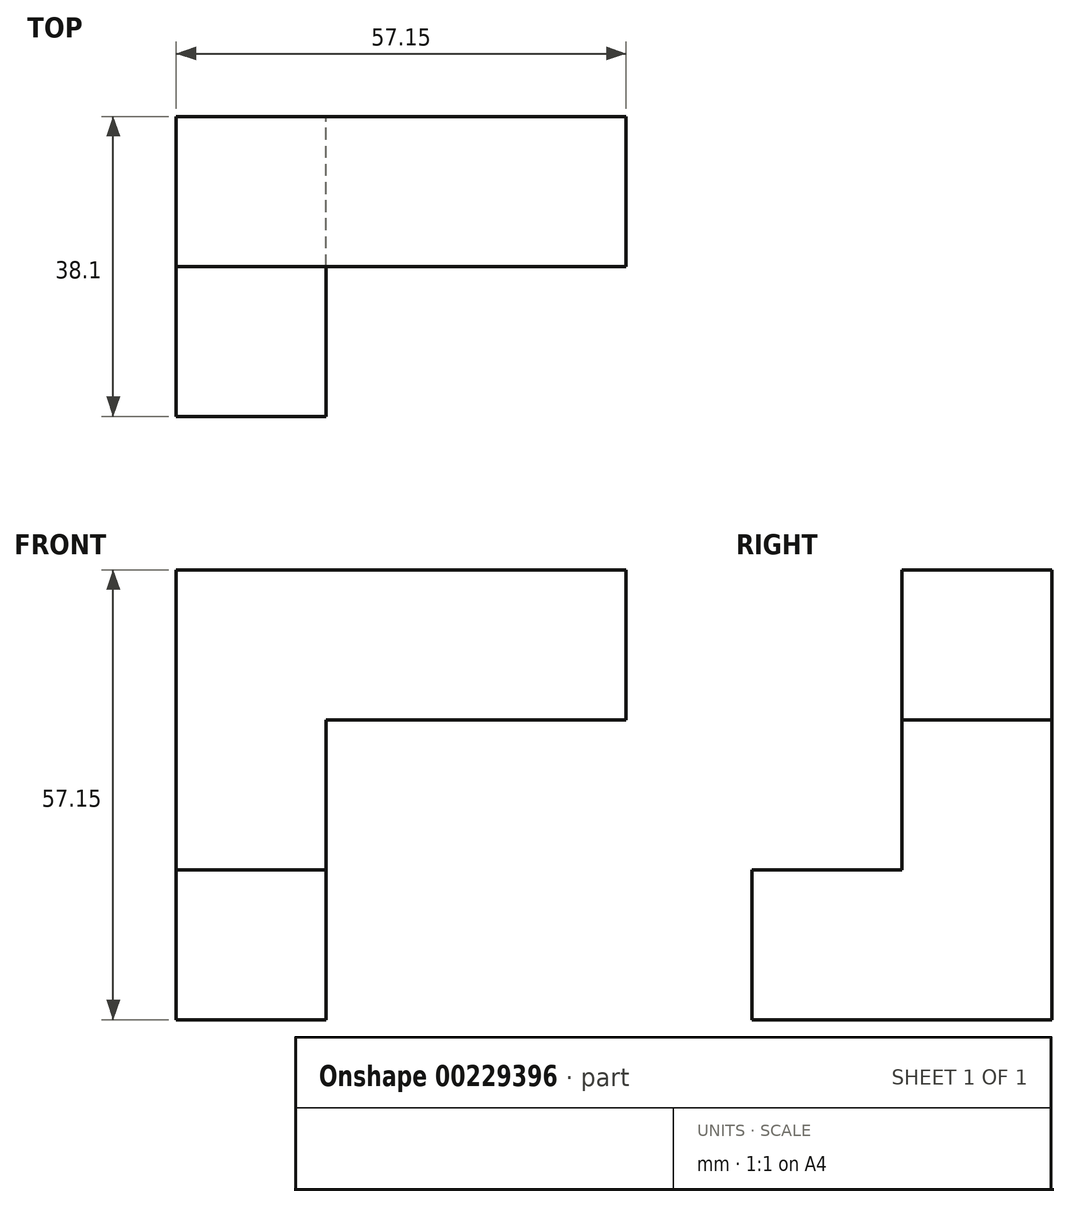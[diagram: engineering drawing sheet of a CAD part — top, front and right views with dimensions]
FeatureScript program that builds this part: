
annotation { "Feature Type Name" : "Feature", "Feature Type Description" : "" }
export const myFeature = defineFeature(function(context is Context, id is Id, definition is map)
    precondition{}
    {
        {
            var Q0;
            Q0=qCreatedBy(makeId("Front.planeOp"),FACE);
            var sketch = newSketch(context, id + "F0", { "sketchPlane" : qUnion([Q0])});
            skLineSegment(sketch, "E0.bottom", {"start": v(-19.05, 27.68) * mm, "end": v(0, 27.68) * mm});
            skLineSegment(sketch, "E0.top", {"start": v(-19.05, -29.47) * mm, "end": v(0, -29.47) * mm});
            skLineSegment(sketch, "E0.left", {"start": v(-19.05, 27.68) * mm, "end": v(-19.05, -29.47) * mm});
            skLineSegment(sketch, "E0.right", {"start": v(0, 27.68) * mm, "end": v(0, -29.47) * mm});
            skLineSegment(sketch, "E1.bottom", {"start": v(0, 27.68) * mm, "end": v(38.1, 27.68) * mm});
            skLineSegment(sketch, "E1.top", {"start": v(0, 8.63) * mm, "end": v(38.1, 8.63) * mm});
            skLineSegment(sketch, "E1.left", {"start": v(0, 27.68) * mm, "end": v(0, 8.63) * mm});
            skLineSegment(sketch, "E1.right", {"start": v(38.1, 27.68) * mm, "end": v(38.1, 8.63) * mm});
            skSolve(sketch);
        }
        {
            var Q0;
            Q0=makeQuery(id+"F0.imprint","IMPRINT",FACE,{"disambiguationData":[TD([[makeQuery(id+"F0.imprint","IMPRINT",EDGE,{"derivedFrom":sQuery(id+"F0.wireOp",EDGE,"E1.bottom")}),-1.0]])]});
            var Q1;
            Q1=makeQuery(id+"F0.imprint","IMPRINT",FACE,{"disambiguationData":[TD([[makeQuery(id+"F0.imprint","IMPRINT",EDGE,{"derivedFrom":sQuery(id+"F0.wireOp",EDGE,"E0.bottom")}),-1.0]])]});
            extrude(context, id + "F1", {"entities" : qUnion([Q0, Q1]), "depth" : 19.05 * mm});
        }
        {
            var Q0;
            Q0=makeQuery(id+"F1.opExtrude","CAP_FACE",FACE,{"disambiguationData":[OSD([sQuery(id+"F0.wireOp",EDGE,"E0.bottom"),sQuery(id+"F0.wireOp",EDGE,"E0.top"),sQuery(id+"F0.wireOp",EDGE,"E0.left"),sQuery(id+"F0.wireOp",EDGE,"E0.right"),sQuery(id+"F0.wireOp",EDGE,"E1.bottom"),sQuery(id+"F0.wireOp",EDGE,"E1.top"),sQuery(id+"F0.wireOp",EDGE,"E1.right")])],"isStart":false});
            var sketch = newSketch(context, id + "F2", { "sketchPlane" : qUnion([Q0])});
            skLineSegment(sketch, "E2.bottom", {"start": v(-19.05, -29.47) * mm, "end": v(0, -29.47) * mm});
            skLineSegment(sketch, "E2.top", {"start": v(-19.05, -10.42) * mm, "end": v(0, -10.42) * mm});
            skLineSegment(sketch, "E2.left", {"start": v(-19.05, -29.47) * mm, "end": v(-19.05, -10.42) * mm});
            skLineSegment(sketch, "E2.right", {"start": v(0, -29.47) * mm, "end": v(0, -10.42) * mm});
            skSolve(sketch);
        }
        {
            var Q0;
            Q0=makeQuery(id+"F2.imprint","IMPRINT",FACE,{"disambiguationData":[TD([[makeQuery(id+"F2.imprint","IMPRINT",EDGE,{"derivedFrom":sQuery(id+"F2.wireOp",EDGE,"E2.bottom")}),1.0]])]});
            extrude(context, id + "F3", {"entities" : qUnion([Q0]), "operationType" : NewBodyOperationType.ADD, "depth" : 19.05 * mm});
        }
    });
